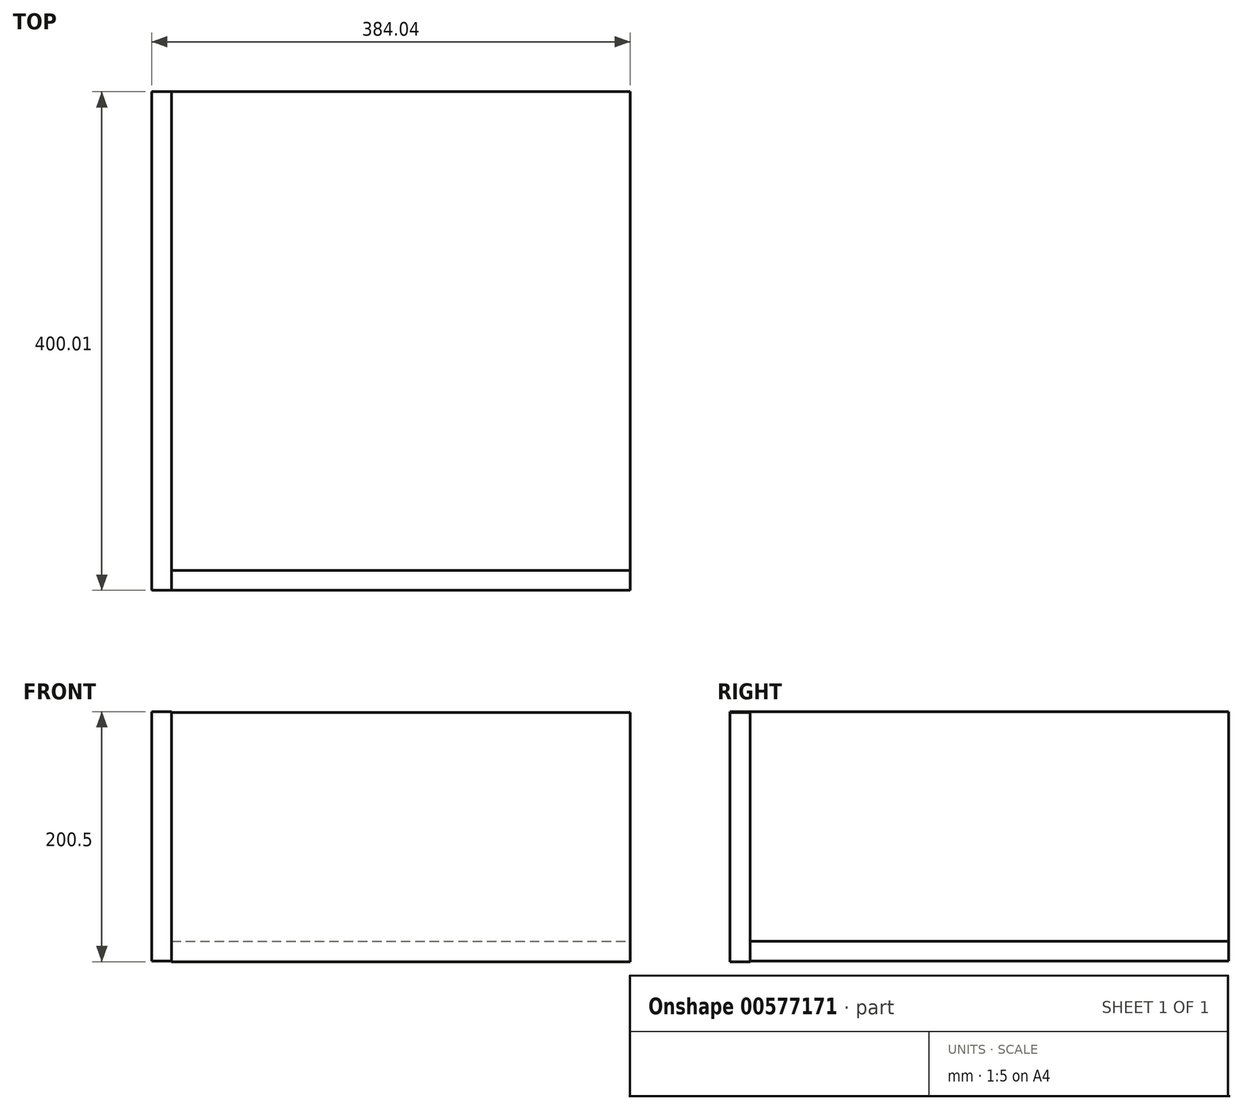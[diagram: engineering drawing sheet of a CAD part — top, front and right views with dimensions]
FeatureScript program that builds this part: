
annotation { "Feature Type Name" : "Feature", "Feature Type Description" : "" }
export const myFeature = defineFeature(function(context is Context, id is Id, definition is map)
    precondition{}
    {
        {
            var Q0;
            Q0=qCreatedBy(makeId("Front.planeOp"),FACE);
            var sketch = newSketch(context, id + "F0", { "sketchPlane" : qUnion([Q0])});
            skLineSegment(sketch, "E0.bottom", {"start": v(-59.04, 137.27) * mm, "end": v(-43.04, 137.27) * mm});
            skLineSegment(sketch, "E0.top", {"start": v(-59.04, -62.73) * mm, "end": v(-43.04, -62.73) * mm});
            skLineSegment(sketch, "E0.left", {"start": v(-59.04, 137.27) * mm, "end": v(-59.04, -62.73) * mm});
            skLineSegment(sketch, "E0.right", {"start": v(-43.04, 137.27) * mm, "end": v(-43.04, -62.73) * mm});
            skLineSegment(sketch, "E1.bottom", {"start": v(-43.04, -62.73) * mm, "end": v(324.96, -62.73) * mm});
            skLineSegment(sketch, "E1.top", {"start": v(-43.04, -46.73) * mm, "end": v(324.96, -46.73) * mm});
            skLineSegment(sketch, "E1.left", {"start": v(-43.04, -62.73) * mm, "end": v(-43.04, -46.73) * mm});
            skLineSegment(sketch, "E1.right", {"start": v(324.96, -62.73) * mm, "end": v(324.96, -46.73) * mm});
            skSolve(sketch);
        }
        {
            var Q0;
            Q0=makeQuery(id+"F0.imprint","IMPRINT",FACE,{"disambiguationData":[TD([[makeQuery(id+"F0.imprint","IMPRINT",EDGE,{"derivedFrom":sQuery(id+"F0.wireOp",EDGE,"E1.bottom")}),1.0]])]});
            extrude(context, id + "F1", {"entities" : qUnion([Q0]), "depth" : 384 * mm, "offsetDistance" : 25 * mm});
        }
        {
            var Q0;
            Q0=makeQuery(id+"F0.imprint","IMPRINT",FACE,{"disambiguationData":[TD([[makeQuery(id+"F0.imprint","IMPRINT",EDGE,{"derivedFrom":sQuery(id+"F0.wireOp",EDGE,"E0.bottom")}),-1.0]])]});
            extrude(context, id + "F2", {"entities" : qUnion([Q0]), "operationType" : NewBodyOperationType.ADD, "depth" : 400 * mm, "offsetDistance" : 25 * mm});
        }
        {
            var Q0;
            Q0=qCreatedBy(makeId("Right.planeOp"),FACE);
            var sketch = newSketch(context, id + "F3", { "sketchPlane" : qUnion([Q0])});
            skLineSegment(sketch, "E2.bottom", {"start": v(-400.01, 136.77) * mm, "end": v(-384.01, 136.77) * mm});
            skLineSegment(sketch, "E2.top", {"start": v(-400.01, -63.23) * mm, "end": v(-384.01, -63.23) * mm});
            skLineSegment(sketch, "E2.left", {"start": v(-400.01, 136.77) * mm, "end": v(-400.01, -63.23) * mm});
            skLineSegment(sketch, "E2.right", {"start": v(-384.01, 136.77) * mm, "end": v(-384.01, -63.23) * mm});
            skSolve(sketch);
        }
        {
            var Q0;
            Q0=makeQuery(id+"F3.imprint","IMPRINT",FACE,{"disambiguationData":[TD([[makeQuery(id+"F3.imprint","IMPRINT",EDGE,{"derivedFrom":sQuery(id+"F3.wireOp",EDGE,"E2.bottom")}),-1.0]])]});
            extrude(context, id + "F4", {"entities" : qUnion([Q0]), "depth" : 325 * mm, "offsetDistance" : 25 * mm, "hasSecondDirection" : true, "secondDirectionOppositeDirection" : true, "secondDirectionDepth" : 43 * mm});
        }
    });
